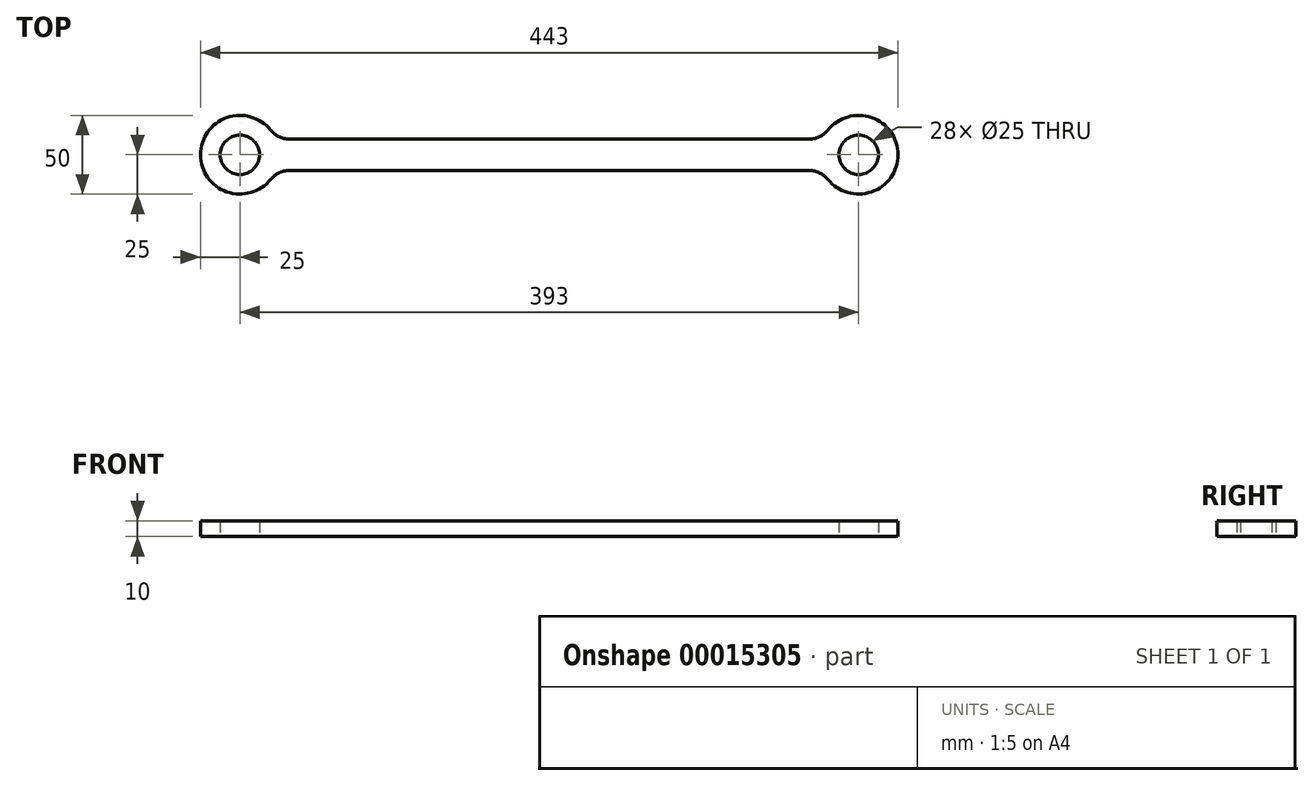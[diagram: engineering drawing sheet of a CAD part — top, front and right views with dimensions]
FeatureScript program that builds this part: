
annotation { "Feature Type Name" : "Feature", "Feature Type Description" : "" }
export const myFeature = defineFeature(function(context is Context, id is Id, definition is map)
    precondition{}
    {
        {
            var Q0;
            Q0=qCreatedBy(makeId("Top.planeOp"),FACE);
            var sketch = newSketch(context, id + "F0", { "sketchPlane" : qUnion([Q0])});
            skArc(sketch, "E0", {"start": v(19.52, 15.63) * mm, "mid": v(-25, 0) * mm, "end": v(19.52, -15.63) * mm});
            skArc(sketch, "E1", {"start": v(373.48, -15.63) * mm, "mid": v(418, 0) * mm, "end": v(373.48, 15.63) * mm});
            skLineSegment(sketch, "E2", {"start": v(31.22, 10) * mm, "end": v(361.78, 10) * mm});
            skLineSegment(sketch, "E3", {"start": v(0, 0) * mm, "end": v(393, 0) * mm, "construction": true});
            skLineSegment(sketch, "E4.MirrorCS", {"start": v(31.22, -10) * mm, "end": v(361.78, -10) * mm});
            skPoint(sketch, "E5.visualSharp", {"position": v(22.91, 10) * mm});
            skArc(sketch, "E5.filletArc", {"start": v(19.52, 15.62) * mm, "mid": v(24.73, 11.48) * mm, "end": v(31.22, 10) * mm});
            skPoint(sketch, "E6.visualSharp", {"position": v(22.91, -10) * mm});
            skArc(sketch, "E6.filletArc", {"start": v(31.22, -10) * mm, "mid": v(24.73, -11.48) * mm, "end": v(19.52, -15.62) * mm});
            skPoint(sketch, "E7.visualSharp", {"position": v(370.09, -10) * mm});
            skArc(sketch, "E7.filletArc", {"start": v(373.48, -15.63) * mm, "mid": v(368.27, -11.48) * mm, "end": v(361.78, -10) * mm});
            skPoint(sketch, "E8.visualSharp", {"position": v(370.09, 10) * mm});
            skArc(sketch, "E8.filletArc", {"start": v(361.78, 10) * mm, "mid": v(368.27, 11.48) * mm, "end": v(373.48, 15.63) * mm});
            skCircle(sketch, "E9", {"center": v(0, 0) * mm, "radius": 12.5 * mm});
            skCircle(sketch, "E10", {"center": v(393, 0) * mm, "radius": 12.5 * mm});
            skSolve(sketch);
        }
        {
            var Q0;
            Q0=qSketchRegion(id+"F0",true);
            extrude(context, id + "F1", {"entities" : qUnion([Q0]), "depth" : 10 * mm});
        }
    });
